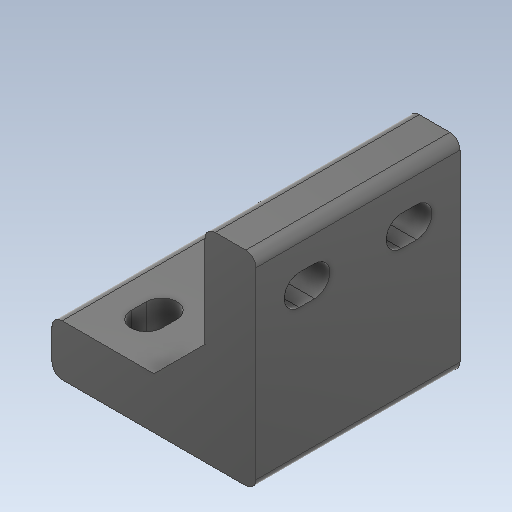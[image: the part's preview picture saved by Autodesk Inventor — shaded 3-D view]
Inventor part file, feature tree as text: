
AUTODESK INVENTOR PART (.ipt)
format: ipt  version: 2020 (Build 240168000, 168)  size: 176,128 bytes
history: native  units: mm
features: extrude x3, sketch x3, chamfer x1, fillet x1
ambient origin geometry x8: Origin, YZ Plane, XZ Plane, XY Plane, X Axis, Y Axis, Z Axis, Center Point
bodies: Solid1 (feature_tree)
feature tree (8):
  extrude  "Extrusion1"  Depth=40.0mm
  extrude  "Extrusion2"  Depth=40.0mm TaperAngle=0.0deg
  extrude  "Extrusion3"  Depth=3.0mm
  chamfer  "Chamfer1"  Distance=10.0mm
  fillet  "Fillet1"  Radius=10.0mm
  sketch  "Sketch1"  dims[d0=10.0mm d1=40.0mm]
  sketch  "Sketch2"  dims[d2=40.0mm d3=40.0mm d4=0.0mm]
  sketch  "Sketch3"  dims[d5=6.0mm d6=3.0mm d7=10.0mm d8=10.0mm d9=0.0mm d10=0.0mm d11=3.0mm d12=6.0mm d13=10.0mm d14=10.0mm d15=0.0mm d16=0.0mm d17=10.0mm d18=2.0mm d19=45.0deg d20=2.0mm]
